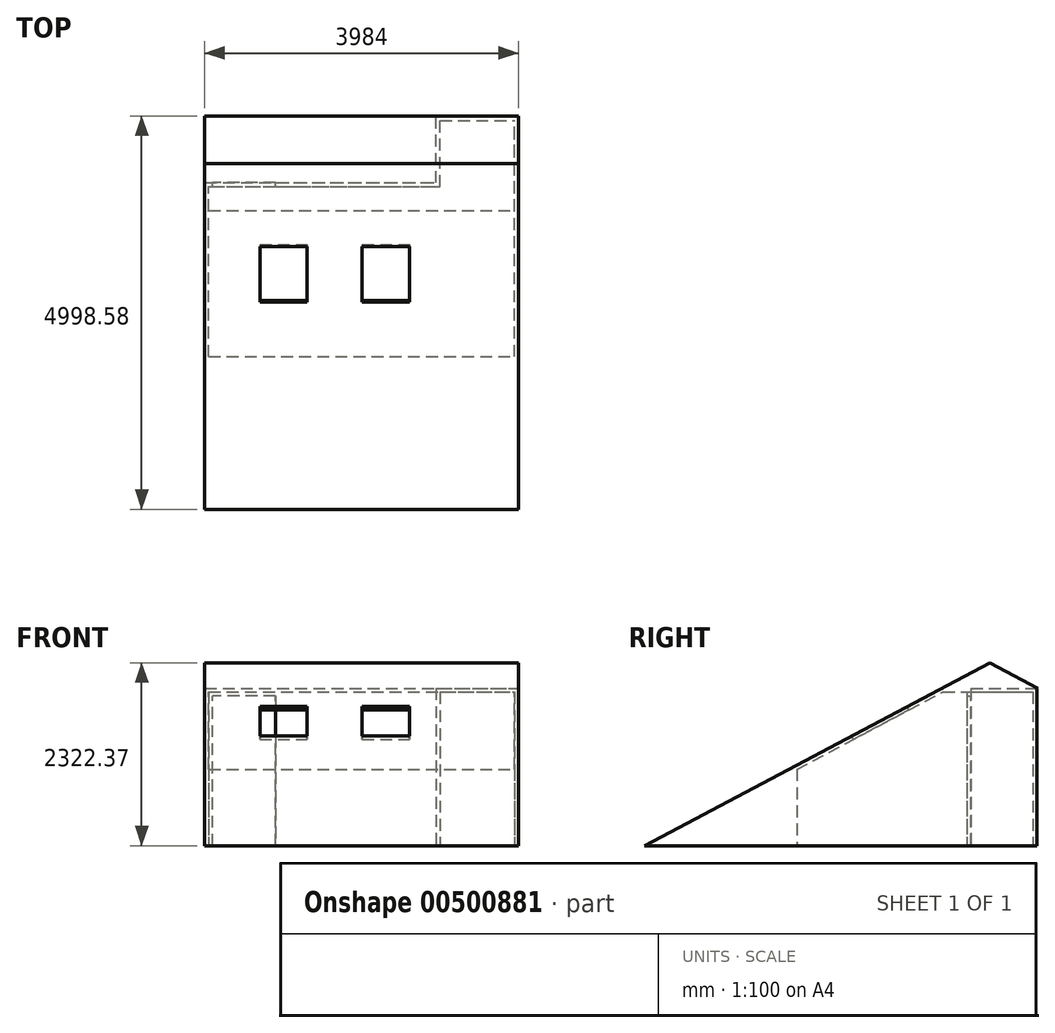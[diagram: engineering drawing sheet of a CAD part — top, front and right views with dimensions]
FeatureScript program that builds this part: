
annotation { "Feature Type Name" : "Feature", "Feature Type Description" : "" }
export const myFeature = defineFeature(function(context is Context, id is Id, definition is map)
    precondition{}
    {
        {
            var Q0;
            Q0=qCreatedBy(makeId("Top.planeOp"),FACE);
            var sketch = newSketch(context, id + "F0", { "sketchPlane" : qUnion([Q0])});
            skLineSegment(sketch, "E0.bottom", {"start": v(0, 0) * mm, "end": v(3984, 0) * mm});
            skLineSegment(sketch, "E0.top", {"start": v(2940, 3098) * mm, "end": v(3984, 3098) * mm});
            skLineSegment(sketch, "E0.left", {"start": v(0, 0) * mm, "end": v(0, 2258) * mm});
            skLineSegment(sketch, "E0.right", {"start": v(3984, 0) * mm, "end": v(3984, 3098) * mm});
            skLineSegment(sketch, "E1", {"start": v(0, 2258) * mm, "end": v(2940, 2258) * mm});
            skLineSegment(sketch, "E2", {"start": v(2940, 2258) * mm, "end": v(2940, 3098) * mm});
            skSolve(sketch);
        }
        {
            var Q0;
            Q0 = qSketchRegion(id + "F0", true);
            extrude(context, id + "F1", {"entities" : qUnion([Q0]), "depth" : 2500 * mm});
        }
        {
            var Q0;
            Q0=makeQuery(id+"F1.opExtrude","SWEPT_FACE",FACE,{"disambiguationData":[OSD([sQuery(id+"F0.wireOp",EDGE,"E0.right")])]});
            var sketch = newSketch(context, id + "F2", { "sketchPlane" : qUnion([Q0])});
            skLineSegment(sketch, "E3", {"start": v(0, 1000) * mm, "end": v(1890, 2000) * mm});
            skLineSegment(sketch, "E4", {"start": v(1890, 2000) * mm, "end": v(3098, 2000) * mm});
            skLineSegment(sketch, "E5", {"start": v(3098, 2000) * mm, "end": v(3098, 2500) * mm});
            skLineSegment(sketch, "E6", {"start": v(3098, 2500) * mm, "end": v(0, 2500) * mm});
            skLineSegment(sketch, "E7", {"start": v(0, 2500) * mm, "end": v(0, 1000) * mm});
            skSolve(sketch);
        }
        {
            var Q0;
            Q0 = qSketchRegion(id + "F2", true);
            extrude(context, id + "F3", {"entities" : qUnion([Q0]), "operationType" : NewBodyOperationType.REMOVE, "endBound" : BoundingType.UP_TO_NEXT, "oppositeDirection" : true, "depth" : 25 * mm});
        }
        {
            var Q0;
            Q0=makeQuery(id+"F1.opExtrude","CAP_FACE",FACE,{"disambiguationData":[OSD([sQuery(id+"F0.wireOp",EDGE,"E0.bottom"),sQuery(id+"F0.wireOp",EDGE,"E0.top"),sQuery(id+"F0.wireOp",EDGE,"E0.left"),sQuery(id+"F0.wireOp",EDGE,"E0.right"),sQuery(id+"F0.wireOp",EDGE,"E1"),sQuery(id+"F0.wireOp",EDGE,"E2")])],"isStart":true});
            shell(context, id + "F4", {"entities" : qUnion([Q0]), "thickness" : 50 * mm});
        }
        {
            var Q0;
            Q0=makeQuery(id+"F1.opExtrude","SWEPT_FACE",FACE,{"disambiguationData":[OSD([sQuery(id+"F0.wireOp",EDGE,"E1")])]});
            var sketch = newSketch(context, id + "F5", { "sketchPlane" : qUnion([Q0])});
            skLineSegment(sketch, "E8.bottom", {"start": v(-900, 0) * mm, "end": v(-100, 0) * mm});
            skLineSegment(sketch, "E8.top", {"start": v(-900, 1900) * mm, "end": v(-100, 1900) * mm});
            skLineSegment(sketch, "E8.left", {"start": v(-900, 0) * mm, "end": v(-900, 1900) * mm});
            skLineSegment(sketch, "E8.right", {"start": v(-100, 0) * mm, "end": v(-100, 1900) * mm});
            skSolve(sketch);
        }
        {
            var Q0;
            Q0 = qSketchRegion(id + "F5", true);
            extrude(context, id + "F6", {"entities" : qUnion([Q0]), "operationType" : NewBodyOperationType.REMOVE, "endBound" : BoundingType.UP_TO_NEXT, "oppositeDirection" : true, "depth" : 25 * mm});
        }
        {
            var Q0;
            Q0=makeQuery(id+"F3.boolean.opBoolean","COPY",FACE,{"derivedFrom":makeQuery(id+"F3.opExtrude","SWEPT_FACE",FACE,{"disambiguationData":[OSD([sQuery(id+"F2.wireOp",EDGE,"E3")])]})});
            var sketch = newSketch(context, id + "F7", { "sketchPlane" : qUnion([Q0])});
            skLineSegment(sketch, "E9.bottom", {"start": v(700, 2105.92) * mm, "end": v(1300, 2105.92) * mm});
            skLineSegment(sketch, "E9.top", {"start": v(700, 1305.92) * mm, "end": v(1300, 1305.92) * mm});
            skLineSegment(sketch, "E9.left", {"start": v(700, 2105.92) * mm, "end": v(700, 1305.92) * mm});
            skLineSegment(sketch, "E9.right", {"start": v(1300, 2105.92) * mm, "end": v(1300, 1305.92) * mm});
            skLineSegment(sketch, "E10.bottom", {"start": v(2000, 2105.92) * mm, "end": v(2600, 2105.92) * mm});
            skLineSegment(sketch, "E10.top", {"start": v(2000, 1305.92) * mm, "end": v(2600, 1305.92) * mm});
            skLineSegment(sketch, "E10.left", {"start": v(2000, 2105.92) * mm, "end": v(2000, 1305.92) * mm});
            skLineSegment(sketch, "E10.right", {"start": v(2600, 2105.92) * mm, "end": v(2600, 1305.92) * mm});
            skSolve(sketch);
        }
        {
            var Q0;
            Q0 = qSketchRegion(id + "F7", true);
            extrude(context, id + "F8", {"entities" : qUnion([Q0]), "operationType" : NewBodyOperationType.REMOVE, "endBound" : BoundingType.UP_TO_NEXT, "oppositeDirection" : true, "depth" : 25 * mm, "offsetDistance" : 25 * mm});
        }
        {
            var Q0;
            Q0=makeQuery(id+"F1.opExtrude","SWEPT_FACE",FACE,{"disambiguationData":[OSD([sQuery(id+"F0.wireOp",EDGE,"E0.right")])]});
            var sketch = newSketch(context, id + "F9", { "sketchPlane" : qUnion([Q0])});
            skLineSegment(sketch, "E11", {"start": v(0, 1000) * mm, "end": v(-1890, 0) * mm});
            skLineSegment(sketch, "E12", {"start": v(-1890, 0) * mm, "end": v(0, 0) * mm});
            skLineSegment(sketch, "E13", {"start": v(0, 0) * mm, "end": v(0, 1000) * mm});
            skLineSegment(sketch, "E14", {"start": v(1890, 2000) * mm, "end": v(2499.29, 2322.37) * mm});
            skLineSegment(sketch, "E15", {"start": v(2499.29, 2322.37) * mm, "end": v(3108.58, 2000) * mm});
            skLineSegment(sketch, "E16", {"start": v(1890, 2000) * mm, "end": v(3108.58, 2000) * mm});
            skSolve(sketch);
        }
        {
            var Q0;
            Q0 = qSketchRegion(id + "F9", true);
            var Q1;
            Q1=makeQuery(id+"F1.opExtrude","SWEPT_FACE",FACE,{"disambiguationData":[OSD([sQuery(id+"F0.wireOp",EDGE,"E0.left")])]});
            extrude(context, id + "F10", {"entities" : qUnion([Q0]), "operationType" : NewBodyOperationType.ADD, "endBound" : BoundingType.UP_TO_SURFACE, "oppositeDirection" : true, "depth" : 25 * mm, "endBoundEntityFace" : qUnion([Q1]), "offsetDistance" : 25 * mm});
        }
    });
